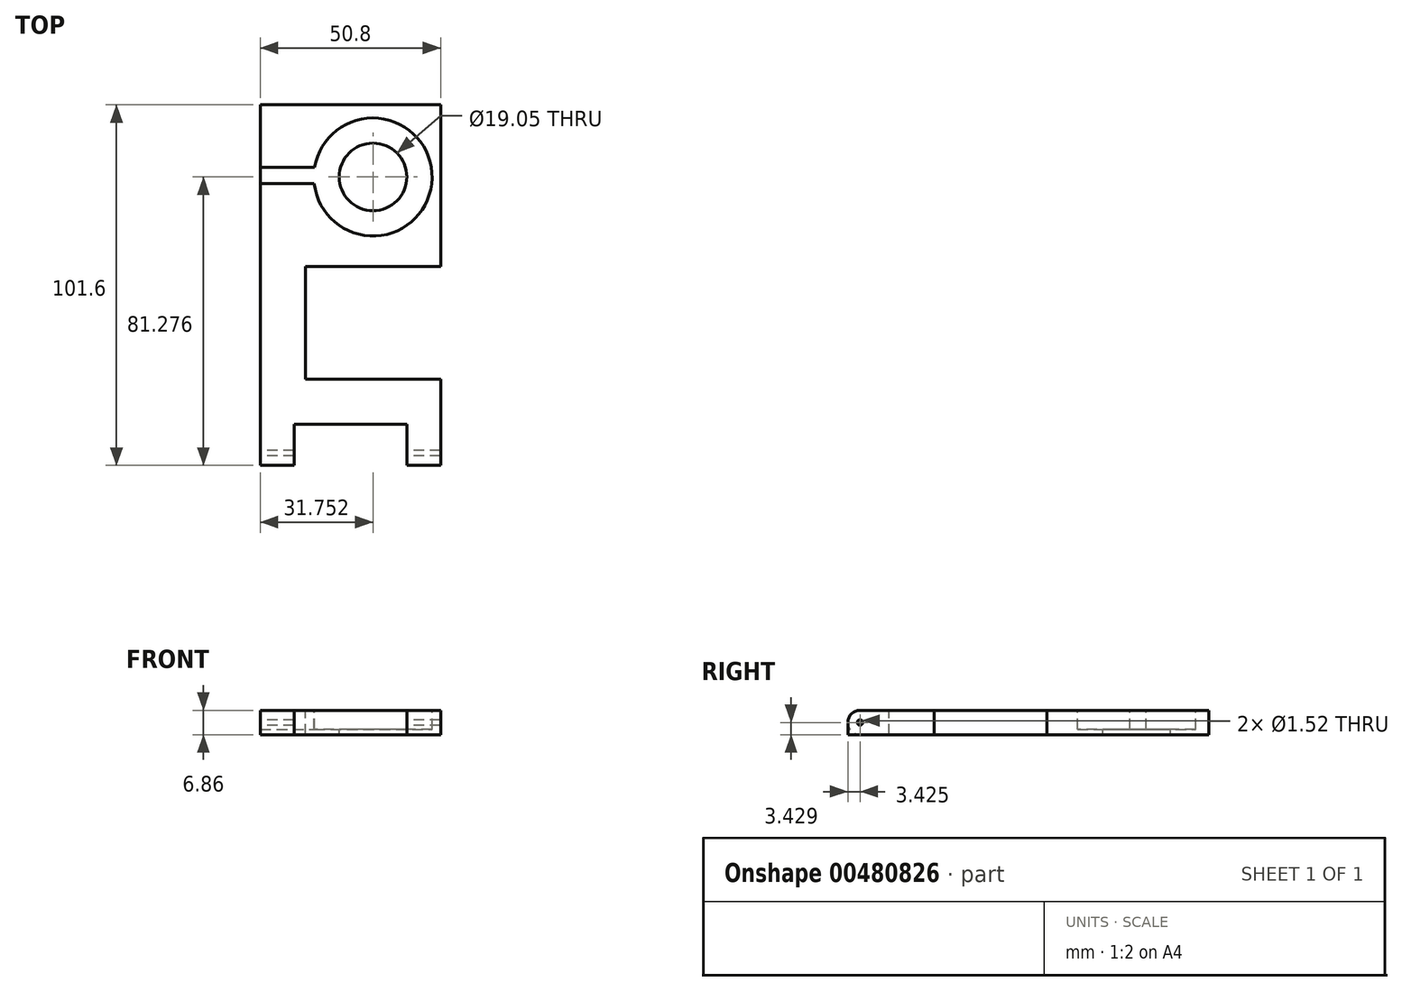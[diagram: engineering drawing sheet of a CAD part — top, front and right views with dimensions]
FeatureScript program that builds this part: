
annotation { "Feature Type Name" : "Feature", "Feature Type Description" : "" }
export const myFeature = defineFeature(function(context is Context, id is Id, definition is map)
    precondition{}
    {
        {
            var Q0;
            Q0=qCreatedBy(makeId("Top.planeOp"),FACE);
            var sketch = newSketch(context, id + "F0", { "sketchPlane" : qUnion([Q0])});
            skLineSegment(sketch, "E0.bottom", {"start": v(-19.32, 72.06) * mm, "end": v(31.48, 72.06) * mm});
            skLineSegment(sketch, "E0.top", {"start": v(-19.32, -29.54) * mm, "end": v(31.48, -29.54) * mm});
            skLineSegment(sketch, "E0.left", {"start": v(-19.32, 72.06) * mm, "end": v(-19.32, -29.54) * mm});
            skLineSegment(sketch, "E0.right", {"start": v(31.48, 72.06) * mm, "end": v(31.48, -29.54) * mm});
            skSolve(sketch);
        }
        {
            var Q0;
            Q0=makeQuery(id+"F0.imprint","IMPRINT",FACE,{"disambiguationData":[TD([[makeQuery(id+"F0.imprint","IMPRINT",EDGE,{"derivedFrom":sQuery(id+"F0.wireOp",EDGE,"E0.bottom")}),-1.0]])]});
            extrude(context, id + "F1", {"entities" : qUnion([Q0]), "depth" : 6.86 * mm});
        }
        {
            var Q0;
            Q0=makeQuery(id+"F1.opExtrude","CAP_FACE",FACE,{"disambiguationData":[OSD([sQuery(id+"F0.wireOp",EDGE,"E0.bottom"),sQuery(id+"F0.wireOp",EDGE,"E0.top"),sQuery(id+"F0.wireOp",EDGE,"E0.left"),sQuery(id+"F0.wireOp",EDGE,"E0.right")])],"isStart":false});
            var sketch = newSketch(context, id + "F2", { "sketchPlane" : qUnion([Q0])});
            skCircle(sketch, "E1", {"center": v(12.43, 51.74) * mm, "radius": 16.64 * mm});
            skSolve(sketch);
        }
        {
            var Q0;
            Q0=makeQuery(id+"F2.imprint","IMPRINT",FACE,{"disambiguationData":[TD([[makeQuery(id+"F2.imprint","IMPRINT",EDGE,{"derivedFrom":sQuery(id+"F2.wireOp",EDGE,"E1")}),1.0]])]});
            extrude(context, id + "F3", {"entities" : qUnion([Q0]), "operationType" : NewBodyOperationType.REMOVE, "oppositeDirection" : true, "depth" : 5.33 * mm});
        }
        {
            var Q0;
            Q0=makeQuery(id+"F3.boolean.opBoolean","COPY",FACE,{"derivedFrom":makeQuery(id+"F3.opExtrude","CAP_FACE",FACE,{"disambiguationData":[OSD([sQuery(id+"F2.wireOp",EDGE,"E1")])],"isStart":false})});
            var sketch = newSketch(context, id + "F4", { "sketchPlane" : qUnion([Q0])});
            skCircle(sketch, "E2", {"center": v(12.43, 51.74) * mm, "radius": 9.53 * mm});
            skSolve(sketch);
        }
        {
            var Q0;
            Q0=makeQuery(id+"F4.imprint","IMPRINT",FACE,{"disambiguationData":[TD([[makeQuery(id+"F4.imprint","IMPRINT",EDGE,{"derivedFrom":sQuery(id+"F4.wireOp",EDGE,"E2")}),1.0]])]});
            extrude(context, id + "F5", {"entities" : qUnion([Q0]), "operationType" : NewBodyOperationType.REMOVE, "oppositeDirection" : true, "depth" : 25.4 * mm});
        }
        {
            var Q0;
            Q0=makeQuery(id+"F1.opExtrude","CAP_FACE",FACE,{"disambiguationData":[OSD([sQuery(id+"F0.wireOp",EDGE,"E0.bottom"),sQuery(id+"F0.wireOp",EDGE,"E0.top"),sQuery(id+"F0.wireOp",EDGE,"E0.left"),sQuery(id+"F0.wireOp",EDGE,"E0.right")])],"isStart":false});
            var sketch = newSketch(context, id + "F6", { "sketchPlane" : qUnion([Q0])});
            skLineSegment(sketch, "E3.bottom", {"start": v(-9.8, -17.94) * mm, "end": v(21.96, -17.94) * mm});
            skLineSegment(sketch, "E3.top", {"start": v(-9.8, -33.18) * mm, "end": v(21.96, -33.18) * mm});
            skLineSegment(sketch, "E3.left", {"start": v(-9.8, -17.94) * mm, "end": v(-9.8, -33.18) * mm});
            skLineSegment(sketch, "E3.right", {"start": v(21.96, -17.94) * mm, "end": v(21.96, -33.18) * mm});
            skSolve(sketch);
        }
        {
            var Q0;
            {var subQ0=sQuery(id+"F6.wireOp",EDGE,"E3.bottom");Q0=makeQuery(id+"F6.imprint","IMPRINT",FACE,{"disambiguationData":[TD([[makeQuery(id+"F6.imprint","IMPRINT",EDGE,{"derivedFrom":subQ0}),-1.0]])]});}
            extrude(context, id + "F7", {"entities" : qUnion([Q0]), "operationType" : NewBodyOperationType.REMOVE, "oppositeDirection" : true, "depth" : 25.4 * mm});
        }
        {
            var Q0;
            Q0=makeQuery(id+"F1.opExtrude","CAP_FACE",FACE,{"disambiguationData":[OSD([sQuery(id+"F0.wireOp",EDGE,"E0.bottom"),sQuery(id+"F0.wireOp",EDGE,"E0.top"),sQuery(id+"F0.wireOp",EDGE,"E0.left"),sQuery(id+"F0.wireOp",EDGE,"E0.right")])],"isStart":false});
            var sketch = newSketch(context, id + "F8", { "sketchPlane" : qUnion([Q0])});
            skLineSegment(sketch, "E4.bottom", {"start": v(-6.62, 26.51) * mm, "end": v(46.93, 26.51) * mm});
            skLineSegment(sketch, "E4.top", {"start": v(-6.62, -5.24) * mm, "end": v(46.93, -5.24) * mm});
            skLineSegment(sketch, "E4.left", {"start": v(-6.62, 26.51) * mm, "end": v(-6.62, -5.24) * mm});
            skLineSegment(sketch, "E4.right", {"start": v(46.93, 26.51) * mm, "end": v(46.93, -5.24) * mm});
            skSolve(sketch);
        }
        {
            var Q0;
            {var subQ0=sQuery(id+"F8.wireOp",EDGE,"E4.left");Q0=makeQuery(id+"F8.imprint","IMPRINT",FACE,{"disambiguationData":[TD([[makeQuery(id+"F8.imprint","IMPRINT",EDGE,{"derivedFrom":subQ0}),1.0]])]});}
            extrude(context, id + "F9", {"entities" : qUnion([Q0]), "operationType" : NewBodyOperationType.REMOVE, "oppositeDirection" : true, "depth" : 25.4 * mm});
        }
        {
            var Q0;
            {var subQ0=sQuery(id+"F0.wireOp",EDGE,"E0.left");var subQ1=sQuery(id+"F0.wireOp",EDGE,"E0.top");Q0=makeQuery(id+"F7.boolean.opBoolean","SPLIT",EDGE,{"disambiguationData":[TD([makeQuery(id+"F1.opExtrude","SWEPT_FACE",FACE,{"disambiguationData":[OSD([subQ0])]})])],"derivedFrom":makeQuery(id+"F1.opExtrude","CAP_EDGE",EDGE,{"disambiguationData":[OSD([subQ1])],"isStart":false})});}
            var Q1;
            {var subQ0=sQuery(id+"F0.wireOp",EDGE,"E0.right");var subQ1=sQuery(id+"F0.wireOp",EDGE,"E0.top");Q1=makeQuery(id+"F7.boolean.opBoolean","SPLIT",EDGE,{"disambiguationData":[TD([makeQuery(id+"F1.opExtrude","SWEPT_FACE",FACE,{"disambiguationData":[OSD([subQ0])]})])],"derivedFrom":makeQuery(id+"F1.opExtrude","CAP_EDGE",EDGE,{"disambiguationData":[OSD([subQ1])],"isStart":false})});}
            var Q2;
            {var subQ0=sQuery(id+"F0.wireOp",EDGE,"E0.left");var subQ1=sQuery(id+"F0.wireOp",EDGE,"E0.top");Q2=makeQuery(id+"F7.boolean.opBoolean","SPLIT",EDGE,{"disambiguationData":[TD([makeQuery(id+"F1.opExtrude","SWEPT_FACE",FACE,{"disambiguationData":[OSD([subQ0])]})])],"derivedFrom":makeQuery(id+"F1.opExtrude","CAP_EDGE",EDGE,{"disambiguationData":[OSD([subQ1])],"isStart":true})});}
            fillet(context, id + "F10", {"entities" : qUnion([Q0, Q1, Q2]), "radius" : 3.43 * mm, "tangentPropagation" : true, "allowEdgeOverflow" : false});
        }
        {
            var Q0;
            Q0=makeQuery(id+"F1.opExtrude","CAP_FACE",FACE,{"disambiguationData":[OSD([sQuery(id+"F0.wireOp",EDGE,"E0.bottom"),sQuery(id+"F0.wireOp",EDGE,"E0.top"),sQuery(id+"F0.wireOp",EDGE,"E0.left"),sQuery(id+"F0.wireOp",EDGE,"E0.right")])],"isStart":false});
            var sketch = newSketch(context, id + "F11", { "sketchPlane" : qUnion([Q0])});
            skLineSegment(sketch, "E5.bottom", {"start": v(-26.12, 54.4) * mm, "end": v(-0.72, 54.4) * mm});
            skLineSegment(sketch, "E5.top", {"start": v(-26.12, 49.83) * mm, "end": v(-0.72, 49.83) * mm});
            skLineSegment(sketch, "E5.left", {"start": v(-26.12, 54.4) * mm, "end": v(-26.12, 49.83) * mm});
            skLineSegment(sketch, "E5.right", {"start": v(-0.72, 54.4) * mm, "end": v(-0.72, 49.83) * mm});
            skSolve(sketch);
        }
        {
            var Q0;
            {var subQ0=sQuery(id+"F11.wireOp",EDGE,"E5.bottom");var subQ1=makeQuery(id+"F1.opExtrude","CAP_EDGE",EDGE,{"disambiguationData":[OSD([sQuery(id+"F0.wireOp",EDGE,"E0.left")])],"isStart":false});var subQ2=makeQuery(id+"F11.imprint","INTERSECT",VERTEX,{"derivedFrom":[subQ1,subQ0]});Q0=makeQuery(id+"F11.imprint","IMPRINT",FACE,{"disambiguationData":[TD([[makeQuery(id+"F11.imprint","IMPRINT",EDGE,{"disambiguationData":[TD([[subQ2,-1.0]])],"derivedFrom":subQ0}),-1.0]])]});}
            extrude(context, id + "F12", {"entities" : qUnion([Q0]), "operationType" : NewBodyOperationType.REMOVE, "oppositeDirection" : true, "depth" : 5.33 * mm});
        }
        {
            var Q0;
            Q0=makeQuery(id+"F1.opExtrude","SWEPT_FACE",FACE,{"disambiguationData":[OSD([sQuery(id+"F0.wireOp",EDGE,"E0.left")])]});
            var sketch = newSketch(context, id + "F13", { "sketchPlane" : qUnion([Q0])});
            skCircle(sketch, "E6", {"center": v(26.12, 3.43) * mm, "radius": 0.76 * mm});
            skSolve(sketch);
        }
        {
            var Q0;
            Q0=makeQuery(id+"F13.imprint","IMPRINT",FACE,{"disambiguationData":[TD([[makeQuery(id+"F13.imprint","IMPRINT",EDGE,{"derivedFrom":sQuery(id+"F13.wireOp",EDGE,"E6")}),1.0]])]});
            extrude(context, id + "F14", {"entities" : qUnion([Q0]), "operationType" : NewBodyOperationType.REMOVE, "oppositeDirection" : true, "depth" : 50.8 * mm});
        }
    });
